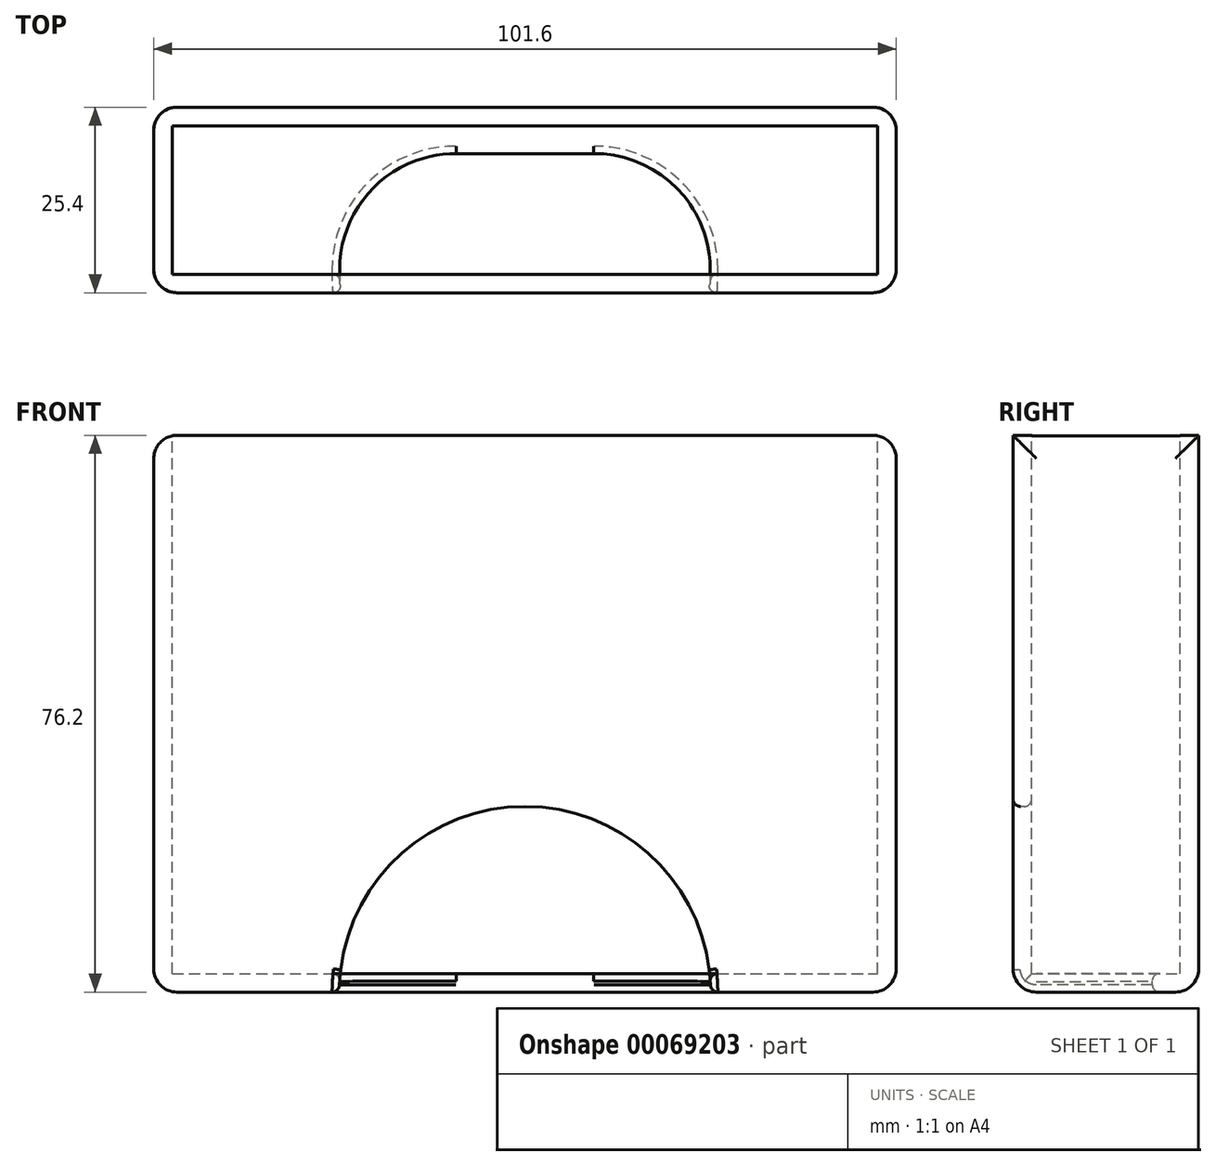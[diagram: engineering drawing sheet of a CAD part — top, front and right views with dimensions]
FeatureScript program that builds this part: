
annotation { "Feature Type Name" : "Feature", "Feature Type Description" : "" }
export const myFeature = defineFeature(function(context is Context, id is Id, definition is map)
    precondition{}
    {
        {
            var Q0;
            Q0=qCreatedBy(makeId("Front.planeOp"),FACE);
            var sketch = newSketch(context, id + "F0", { "sketchPlane" : qUnion([Q0])});
            skLineSegment(sketch, "E0.rect.bottom", {"start": v(-50.8, -38.1) * mm, "end": v(50.8, -38.1) * mm});
            skLineSegment(sketch, "E0.rect.top", {"start": v(-50.8, 38.1) * mm, "end": v(50.8, 38.1) * mm});
            skLineSegment(sketch, "E0.rect.left", {"start": v(-50.8, -38.1) * mm, "end": v(-50.8, 38.1) * mm});
            skLineSegment(sketch, "E0.rect.right", {"start": v(50.8, -38.1) * mm, "end": v(50.8, 38.1) * mm});
            skPoint(sketch, "E0.rect.middle", {"position": v(0, 0) * mm});
            skSolve(sketch);
        }
        {
            var Q0;
            Q0=makeQuery(id+"F0.imprint","IMPRINT",FACE,{"disambiguationData":[TD([[makeQuery(id+"F0.imprint","IMPRINT",EDGE,{"derivedFrom":sQuery(id+"F0.wireOp",EDGE,"E0.rect.bottom")}),1.0]])]});
            extrude(context, id + "F1", {"entities" : qUnion([Q0]), "depth" : 25.4 * mm});
        }
        {
            var Q0;
            Q0=makeQuery(id+"F1.opExtrude","SWEPT_FACE",FACE,{"disambiguationData":[OSD([sQuery(id+"F0.wireOp",EDGE,"E0.rect.top")])]});
            shell(context, id + "F2", {"entities" : qUnion([Q0]), "thickness" : 2.54 * mm});
        }
        {
            var Q0;
            Q0=makeQuery(id+"F1.opExtrude","SWEPT_FACE",FACE,{"disambiguationData":[OSD([sQuery(id+"F0.wireOp",EDGE,"E0.rect.right")])]});
            var Q1;
            Q1=makeQuery(id+"F1.opExtrude","SWEPT_FACE",FACE,{"disambiguationData":[OSD([sQuery(id+"F0.wireOp",EDGE,"E0.rect.left")])]});
            var Q2;
            Q2=makeQuery(id+"F1.opExtrude","SWEPT_FACE",FACE,{"disambiguationData":[OSD([sQuery(id+"F0.wireOp",EDGE,"E0.rect.bottom")])]});
            fillet(context, id + "F3", {"entities" : qUnion([Q0, Q1, Q2]), "radius" : 3.17 * mm, "tangentPropagation" : true, "allowEdgeOverflow" : false});
        }
        {
            var Q0;
            Q0=makeQuery(id+"F1.opExtrude","CAP_FACE",FACE,{"disambiguationData":[OSD([sQuery(id+"F0.wireOp",EDGE,"E0.rect.bottom"),sQuery(id+"F0.wireOp",EDGE,"E0.rect.top"),sQuery(id+"F0.wireOp",EDGE,"E0.rect.left"),sQuery(id+"F0.wireOp",EDGE,"E0.rect.right")])],"isStart":false});
            var sketch = newSketch(context, id + "F4", { "sketchPlane" : qUnion([Q0])});
            skCircle(sketch, "E1", {"center": v(0, -38.1) * mm, "radius": 25.4 * mm});
            skSolve(sketch);
        }
        {
            var Q0;
            {var subQ0=sQuery(id+"F4.wireOp",EDGE,"E1");var subQ1=makeQuery(id+"F1.opExtrude","CAP_EDGE",EDGE,{"disambiguationData":[OSD([sQuery(id+"F0.wireOp",EDGE,"E0.rect.bottom")])],"isStart":false});var subQ2=makeQuery(id+"F4.imprint","INTERSECT",VERTEX,{"disambiguationData":[OD(0.0)],"derivedFrom":[subQ1,subQ0]});Q0=makeQuery(id+"F4.imprint","IMPRINT",FACE,{"disambiguationData":[TD([[makeQuery(id+"F4.imprint","IMPRINT",EDGE,{"disambiguationData":[TD([[subQ2,-1.0]])],"derivedFrom":subQ0}),1.0]])]});}
            var Q1;
            {var subQ0=sQuery(id+"F4.wireOp",EDGE,"E1");var subQ1=makeQuery(id+"F1.opExtrude","CAP_EDGE",EDGE,{"disambiguationData":[OSD([sQuery(id+"F0.wireOp",EDGE,"E0.rect.bottom")])],"isStart":false});var subQ2=makeQuery(id+"F4.imprint","INTERSECT",VERTEX,{"disambiguationData":[OD(0.0)],"derivedFrom":[subQ1,subQ0]});Q1=makeQuery(id+"F4.imprint","IMPRINT",FACE,{"disambiguationData":[TD([[makeQuery(id+"F4.imprint","IMPRINT",EDGE,{"disambiguationData":[TD([[subQ2,1.0]])],"derivedFrom":subQ0}),1.0]])]});}
            extrude(context, id + "F5", {"entities" : qUnion([Q0, Q1]), "operationType" : NewBodyOperationType.REMOVE, "oppositeDirection" : true, "depth" : 19.05 * mm});
        }
        {
            var Q0;
            Q0=makeQuery(id+"F5.boolean.opBoolean","COPY",EDGE,{"disambiguationData":[OD(0.0)],"derivedFrom":makeQuery(id+"F5.opExtrude","CAP_EDGE",EDGE,{"disambiguationData":[OSD([sQuery(id+"F4.wireOp",EDGE,"E1")])],"isStart":false})});
            var Q1;
            Q1=makeQuery(id+"F5.boolean.opBoolean","COPY",EDGE,{"disambiguationData":[OD(1.0)],"derivedFrom":makeQuery(id+"F5.opExtrude","CAP_EDGE",EDGE,{"disambiguationData":[OSD([sQuery(id+"F4.wireOp",EDGE,"E1")])],"isStart":false})});
            fillet(context, id + "F7", {"entities" : qUnion([Q0, Q1]), "radius" : 15.88 * mm, "tangentPropagation" : true, "allowEdgeOverflow" : false});
        }
        {
            var Q0;
            Q0=makeQuery(id+"F5.boolean.opBoolean","COPY",FACE,{"derivedFrom":makeQuery(id+"F5.opExtrude","SWEPT_FACE",FACE,{"disambiguationData":[OSD([sQuery(id+"F4.wireOp",EDGE,"E1")])]})});
            fillet(context, id + "F6", {"entities" : qUnion([Q0]), "radius" : 1.02 * mm, "tangentPropagation" : true, "allowEdgeOverflow" : false});
        }
    });
